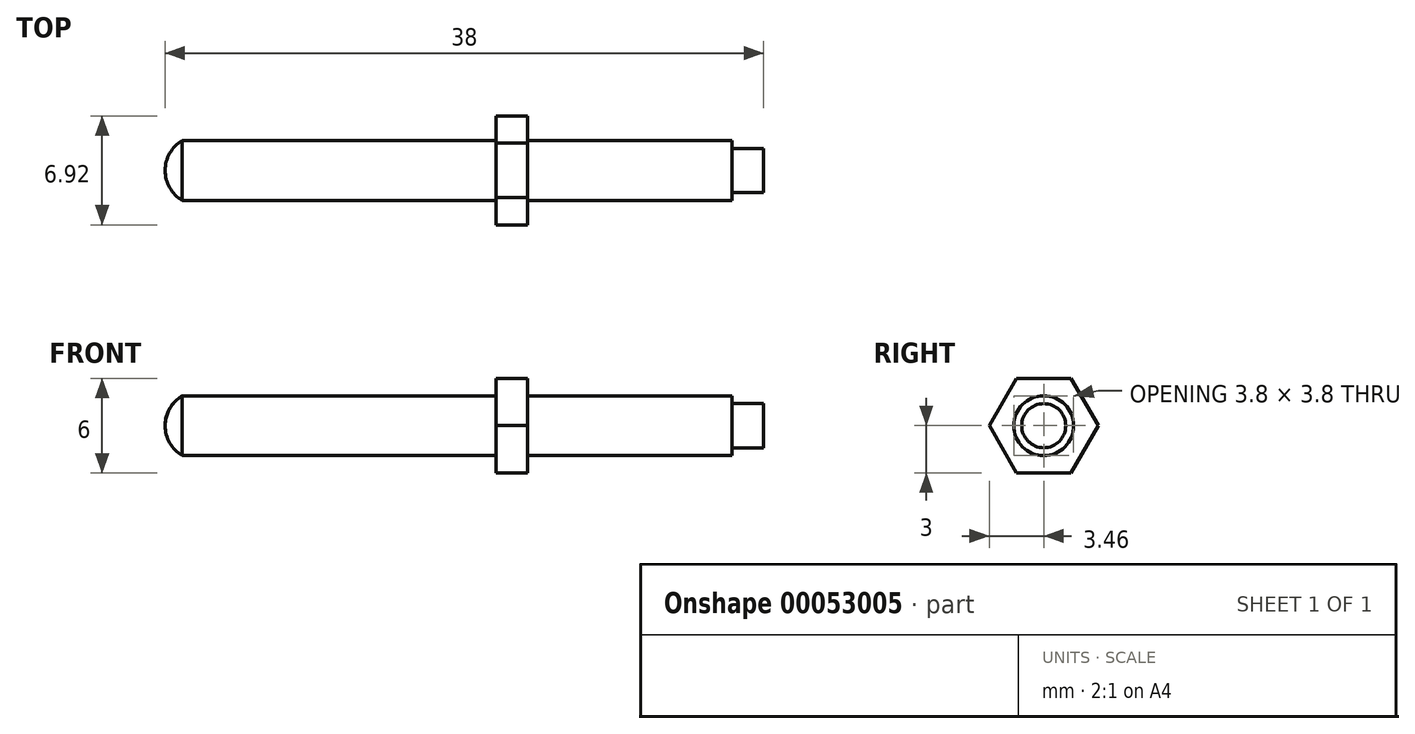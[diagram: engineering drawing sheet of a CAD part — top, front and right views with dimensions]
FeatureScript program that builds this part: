
annotation { "Feature Type Name" : "Feature", "Feature Type Description" : "" }
export const myFeature = defineFeature(function(context is Context, id is Id, definition is map)
    precondition{}
    {
        {
            var Q0;
            Q0=qCreatedBy(makeId("Front.planeOp"),FACE);
            var sketch = newSketch(context, id + "F0", { "sketchPlane" : qUnion([Q0])});
            skLineSegment(sketch, "E0", {"start": v(-21, 0) * mm, "end": v(0, 0) * mm});
            skLineSegment(sketch, "E1", {"start": v(0, 0) * mm, "end": v(17, 0) * mm});
            skLineSegment(sketch, "E2", {"start": v(17, 0) * mm, "end": v(17, 1.4) * mm});
            skLineSegment(sketch, "E3", {"start": v(17, 1.4) * mm, "end": v(15, 1.4) * mm});
            skLineSegment(sketch, "E4", {"start": v(15, 1.4) * mm, "end": v(15, 1.9) * mm});
            skLineSegment(sketch, "E5", {"start": v(15, 1.9) * mm, "end": v(0, 1.9) * mm});
            skLineSegment(sketch, "E6", {"start": v(0, 1.9) * mm, "end": v(-19.9, 1.9) * mm});
            skArc(sketch, "E7", {"start": v(-19.9, 1.9) * mm, "mid": v(-20.7, 1.1) * mm, "end": v(-21, 0) * mm});
            skSolve(sketch);
        }
        {
            var Q0;
            Q0=makeQuery(id+"F0.imprint","IMPRINT",FACE,{"disambiguationData":[TD([[makeQuery(id+"F0.imprint","IMPRINT",EDGE,{"derivedFrom":sQuery(id+"F0.wireOp",EDGE,"E0")}),1.0]])]});
            var Q1;
            Q1=sQuery(id+"F0.wireOp",EDGE,"E0");
            revolve(context, id + "F1", {"entities" : qUnion([Q0]), "axis" : qUnion([Q1]), "revolveType" : RevolveType.FULL});
        }
        {
            var Q0;
            Q0=qCreatedBy(makeId("Right.planeOp"),FACE);
            var sketch = newSketch(context, id + "F2", { "sketchPlane" : qUnion([Q0])});
            skCircle(sketch, "E8.cCircle", {"center": v(0, 0) * mm, "radius": 3 * mm, "construction": true});
            skLineSegment(sketch, "E8.0", {"start": v(3.46, 0) * mm, "end": v(1.73, -3) * mm});
            skLineSegment(sketch, "E8.1", {"start": v(1.73, -3) * mm, "end": v(-1.73, -3) * mm});
            skLineSegment(sketch, "E8.2", {"start": v(-1.73, -3) * mm, "end": v(-3.46, 0) * mm});
            skLineSegment(sketch, "E8.3", {"start": v(-3.46, 0) * mm, "end": v(-1.73, 3) * mm});
            skLineSegment(sketch, "E8.4", {"start": v(-1.73, 3) * mm, "end": v(1.73, 3) * mm});
            skLineSegment(sketch, "E8.5", {"start": v(1.73, 3) * mm, "end": v(3.46, 0) * mm});
            skPoint(sketch, "E8.0.midPoint", {"position": v(2.6, -1.5) * mm});
            skSolve(sketch);
        }
        {
            var Q0;
            Q0=makeQuery(id+"F2.imprint","IMPRINT",FACE,{"disambiguationData":[TD([[makeQuery(id+"F2.imprint","IMPRINT",EDGE,{"derivedFrom":sQuery(id+"F2.wireOp",EDGE,"E8.0")}),-1.0]])]});
            extrude(context, id + "F3", {"entities" : qUnion([Q0]), "operationType" : NewBodyOperationType.ADD, "depth" : 2 * mm});
        }
    });
